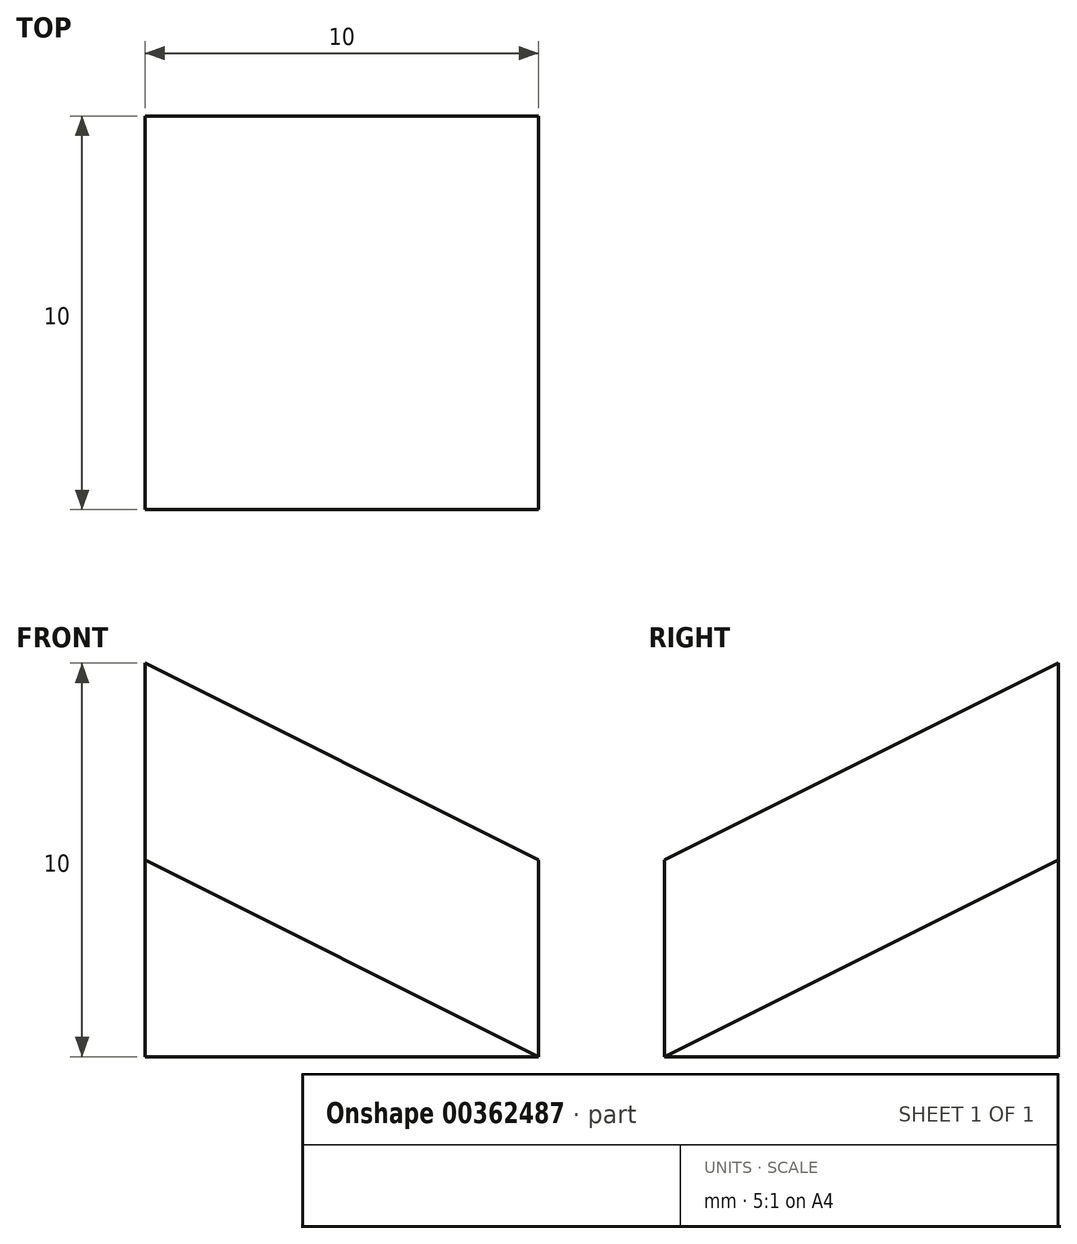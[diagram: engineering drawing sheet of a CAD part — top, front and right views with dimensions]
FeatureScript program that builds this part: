
annotation { "Feature Type Name" : "Feature", "Feature Type Description" : "" }
export const myFeature = defineFeature(function(context is Context, id is Id, definition is map)
    precondition{}
    {
        {
            var Q0;
            Q0=qCreatedBy(makeId("Front.planeOp"),FACE);
            var sketch = newSketch(context, id + "F0", { "sketchPlane" : qUnion([Q0])});
            skLineSegment(sketch, "E0.bottom", {"start": v(0, 0) * mm, "end": v(-10, 0) * mm});
            skLineSegment(sketch, "E0.top", {"start": v(0, 10) * mm, "end": v(-10, 10) * mm});
            skLineSegment(sketch, "E0.left", {"start": v(0, 0) * mm, "end": v(0, 10) * mm});
            skLineSegment(sketch, "E0.right", {"start": v(-10, 0) * mm, "end": v(-10, 10) * mm});
            skSolve(sketch);
        }
        {
            var Q0;
            Q0=qSketchRegion(id+"F0",true);
            extrude(context, id + "F1", {"entities" : qUnion([Q0]), "depth" : 10 * mm});
        }
        {
            var Q0;
            Q0=makeQuery(id+"F1.opExtrude","SWEPT_FACE",FACE,{"disambiguationData":[OSD([sQuery(id+"F0.wireOp",EDGE,"E0.left")])]});
            var sketch = newSketch(context, id + "F2", { "sketchPlane" : qUnion([Q0])});
            skPoint(sketch, "E1", {"position": v(0, 5) * mm});
            skSolve(sketch);
        }
        {
            var Q0;
            Q0=makeQuery(id+"F1.opExtrude","SWEPT_FACE",FACE,{"disambiguationData":[OSD([sQuery(id+"F0.wireOp",EDGE,"E0.top")])]});
            var sketch = newSketch(context, id + "F3", { "sketchPlane" : qUnion([Q0])});
            skPoint(sketch, "E2", {"position": v(-5, 0) * mm});
            skSolve(sketch);
        }
        {
            var Q0;
            Q0=makeQuery(id+"F1.opExtrude","CAP_EDGE",EDGE,{"disambiguationData":[OSD([sQuery(id+"F0.wireOp",EDGE,"E0.right")])],"isStart":false});
            cPoint(context, id + "F4", {"entities" : qUnion([Q0]), "parameter" : 0.5});
        }
        {
            var Q0;
            Q0=sQuery(id+"F2.wireOp",VERTEX,"E1");
            var Q1;
            Q1 = qCreatedBy(id + "F4" ,VERTEX);
            var Q2;
            Q2=makeQuery(id+"F1.opExtrude","CAP_VERTEX",VERTEX,{"disambiguationData":[OSD([sQuery(id+"F0.wireOp",EDGE,"E0.top"),sQuery(id+"F0.wireOp",EDGE,"E0.right")])],"isStart":true});
            cPlane(context, id + "F5", {"entities" : qUnion([Q0, Q1, Q2]), "cplaneType" : CPlaneType.THREE_POINT, "offset" : 25 * mm, "width" : 150 * mm, "height" : 150 * mm});
        }
        {
            var Q0;
            {var subQ0=sQuery(id+"F0.wireOp",EDGE,"E0.top");Q0=makeQuery(id+"F3.imprint","IMPRINT",FACE,{"disambiguationData":[TD([[makeQuery(id+"F3.imprint","IMPRINT",EDGE,{"derivedFrom":makeQuery(id+"F1.opExtrude","CAP_EDGE",EDGE,{"disambiguationData":[OSD([subQ0])],"isStart":true})}),1.0]])]});}
            var Q1;
            Q1=qCreatedBy(id+"F5.planeOp",FACE);
            extrude(context, id + "F6", {"entities" : qUnion([Q0]), "operationType" : NewBodyOperationType.REMOVE, "endBound" : BoundingType.UP_TO_SURFACE, "oppositeDirection" : true, "endBoundEntityFace" : qUnion([Q1]), "depth" : 25 * mm});
        }
    });
